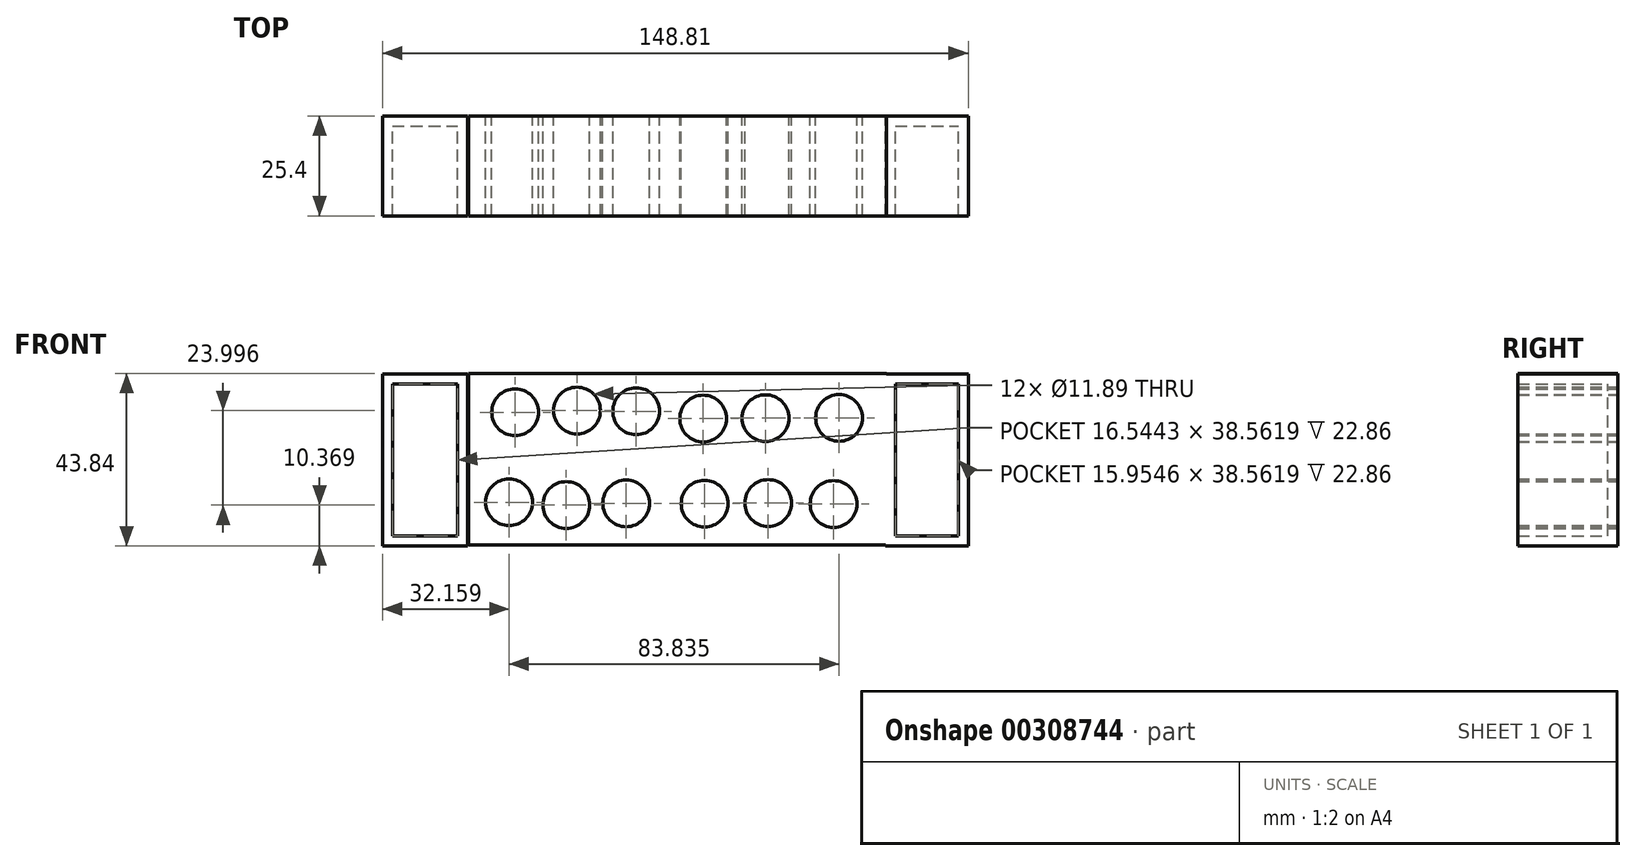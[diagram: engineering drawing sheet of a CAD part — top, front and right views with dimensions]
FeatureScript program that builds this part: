
annotation { "Feature Type Name" : "Feature", "Feature Type Description" : "" }
export const myFeature = defineFeature(function(context is Context, id is Id, definition is map)
    precondition{}
    {
        {
            var Q0;
            Q0=qCreatedBy(makeId("Front.planeOp"),FACE);
            var sketch = newSketch(context, id + "F0", { "sketchPlane" : qUnion([Q0])});
            skLineSegment(sketch, "E0", {"start": v(-61.92, 14.74) * mm, "end": v(86.9, 14.74) * mm});
            skLineSegment(sketch, "E1", {"start": v(86.9, 14.74) * mm, "end": v(86.9, -28.9) * mm});
            skLineSegment(sketch, "E2", {"start": v(86.9, -28.9) * mm, "end": v(-61.92, -28.9) * mm});
            skLineSegment(sketch, "E3", {"start": v(-61.92, -28.9) * mm, "end": v(-61.92, 14.74) * mm});
            skLineSegment(sketch, "E4", {"start": v(-40.3, 14.74) * mm, "end": v(-40.3, -28.9) * mm});
            skLineSegment(sketch, "E5", {"start": v(65.86, -28.9) * mm, "end": v(65.86, 14.74) * mm});
            skSolve(sketch);
        }
        {
            var Q0;
            {var subQ0=sQuery(id+"F0.wireOp",EDGE,"E3");Q0=makeQuery(id+"F0.imprint","IMPRINT",FACE,{"disambiguationData":[TD([[makeQuery(id+"F0.imprint","IMPRINT",EDGE,{"derivedFrom":subQ0}),-1.0]])]});}
            var Q1;
            {var subQ0=sQuery(id+"F0.wireOp",EDGE,"E1");Q1=makeQuery(id+"F0.imprint","IMPRINT",FACE,{"disambiguationData":[TD([[makeQuery(id+"F0.imprint","IMPRINT",EDGE,{"derivedFrom":subQ0}),-1.0]])]});}
            extrude(context, id + "F1", {"entities" : qUnion([Q0, Q1]), "depth" : 25.4 * mm});
        }
        {
            var Q0;
            Q0=makeQuery(id+"F1.opExtrude","CAP_FACE",FACE,{"disambiguationData":[OSD([sQuery(id+"F0.wireOp",EDGE,"E0"),sQuery(id+"F0.wireOp",EDGE,"E1"),sQuery(id+"F0.wireOp",EDGE,"E2"),sQuery(id+"F0.wireOp",EDGE,"E5")])],"isStart":false});
            var Q1;
            Q1=makeQuery(id+"F1.opExtrude","CAP_FACE",FACE,{"disambiguationData":[OSD([sQuery(id+"F0.wireOp",EDGE,"E0"),sQuery(id+"F0.wireOp",EDGE,"E2"),sQuery(id+"F0.wireOp",EDGE,"E3"),sQuery(id+"F0.wireOp",EDGE,"E4")])],"isStart":false});
            shell(context, id + "F2", {"entities" : qUnion([Q0, Q1]), "thickness" : 2.54 * mm});
        }
        {
            var Q0;
            Q0=qCreatedBy(makeId("Front.planeOp"),FACE);
            var sketch = newSketch(context, id + "F3", { "sketchPlane" : qUnion([Q0])});
            skLineSegment(sketch, "E6.bottom", {"start": v(-40.07, 14.94) * mm, "end": v(66.09, 14.94) * mm});
            skLineSegment(sketch, "E6.top", {"start": v(-40.07, -28.7) * mm, "end": v(66.09, -28.7) * mm});
            skLineSegment(sketch, "E6.left", {"start": v(-40.07, 14.94) * mm, "end": v(-40.07, -28.7) * mm});
            skLineSegment(sketch, "E6.right", {"start": v(66.09, 14.94) * mm, "end": v(66.09, -28.7) * mm});
            skSolve(sketch);
        }
        {
            var Q0;
            Q0=makeQuery(id+"F3.imprint","IMPRINT",FACE,{"disambiguationData":[TD([[makeQuery(id+"F3.imprint","IMPRINT",EDGE,{"derivedFrom":sQuery(id+"F3.wireOp",EDGE,"E6.bottom")}),-1.0]])]});
            extrude(context, id + "F4", {"entities" : qUnion([Q0]), "operationType" : NewBodyOperationType.ADD, "depth" : 25.4 * mm});
        }
        {
            var Q0;
            Q0=qCreatedBy(makeId("Front.planeOp"),FACE);
            var sketch = newSketch(context, id + "F5", { "sketchPlane" : qUnion([Q0])});
            skCircle(sketch, "E7", {"center": v(-28.22, 5.05) * mm, "radius": 5.94 * mm});
            skCircle(sketch, "E8", {"center": v(-12.51, 5.47) * mm, "radius": 5.94 * mm});
            skCircle(sketch, "E9", {"center": v(2.54, 5.3) * mm, "radius": 5.94 * mm});
            skCircle(sketch, "E10", {"center": v(19.56, 3.45) * mm, "radius": 5.94 * mm});
            skCircle(sketch, "E11", {"center": v(35.4, 3.55) * mm, "radius": 5.94 * mm});
            skCircle(sketch, "E12", {"center": v(54.07, 3.62) * mm, "radius": 5.94 * mm});
            skCircle(sketch, "E13", {"center": v(-29.76, -17.82) * mm, "radius": 5.94 * mm});
            skCircle(sketch, "E14", {"center": v(-15.23, -18.53) * mm, "radius": 5.94 * mm});
            skCircle(sketch, "E15", {"center": v(0, -18.08) * mm, "radius": 5.94 * mm});
            skCircle(sketch, "E16", {"center": v(19.92, -18.17) * mm, "radius": 5.94 * mm});
            skCircle(sketch, "E17", {"center": v(36.08, -18.02) * mm, "radius": 5.94 * mm});
            skCircle(sketch, "E18", {"center": v(52.68, -18.26) * mm, "radius": 5.94 * mm});
            skSolve(sketch);
        }
        {
            var Q0;
            Q0=makeQuery(id+"F5.imprint","IMPRINT",FACE,{"disambiguationData":[TD([[makeQuery(id+"F5.imprint","IMPRINT",EDGE,{"derivedFrom":sQuery(id+"F5.wireOp",EDGE,"E13")}),1.0]])]});
            var Q1;
            Q1=makeQuery(id+"F5.imprint","IMPRINT",FACE,{"disambiguationData":[TD([[makeQuery(id+"F5.imprint","IMPRINT",EDGE,{"derivedFrom":sQuery(id+"F5.wireOp",EDGE,"E14")}),1.0]])]});
            var Q2;
            Q2=makeQuery(id+"F5.imprint","IMPRINT",FACE,{"disambiguationData":[TD([[makeQuery(id+"F5.imprint","IMPRINT",EDGE,{"derivedFrom":sQuery(id+"F5.wireOp",EDGE,"E15")}),1.0]])]});
            var Q3;
            Q3=makeQuery(id+"F5.imprint","IMPRINT",FACE,{"disambiguationData":[TD([[makeQuery(id+"F5.imprint","IMPRINT",EDGE,{"derivedFrom":sQuery(id+"F5.wireOp",EDGE,"E16")}),1.0]])]});
            var Q4;
            Q4=makeQuery(id+"F5.imprint","IMPRINT",FACE,{"disambiguationData":[TD([[makeQuery(id+"F5.imprint","IMPRINT",EDGE,{"derivedFrom":sQuery(id+"F5.wireOp",EDGE,"E17")}),1.0]])]});
            var Q5;
            Q5=makeQuery(id+"F5.imprint","IMPRINT",FACE,{"disambiguationData":[TD([[makeQuery(id+"F5.imprint","IMPRINT",EDGE,{"derivedFrom":sQuery(id+"F5.wireOp",EDGE,"E18")}),1.0]])]});
            var Q6;
            Q6=makeQuery(id+"F5.imprint","IMPRINT",FACE,{"disambiguationData":[TD([[makeQuery(id+"F5.imprint","IMPRINT",EDGE,{"derivedFrom":sQuery(id+"F5.wireOp",EDGE,"E12")}),1.0]])]});
            var Q7;
            Q7=makeQuery(id+"F5.imprint","IMPRINT",FACE,{"disambiguationData":[TD([[makeQuery(id+"F5.imprint","IMPRINT",EDGE,{"derivedFrom":sQuery(id+"F5.wireOp",EDGE,"E11")}),1.0]])]});
            var Q8;
            Q8=makeQuery(id+"F5.imprint","IMPRINT",FACE,{"disambiguationData":[TD([[makeQuery(id+"F5.imprint","IMPRINT",EDGE,{"derivedFrom":sQuery(id+"F5.wireOp",EDGE,"E10")}),1.0]])]});
            var Q9;
            Q9=makeQuery(id+"F5.imprint","IMPRINT",FACE,{"disambiguationData":[TD([[makeQuery(id+"F5.imprint","IMPRINT",EDGE,{"derivedFrom":sQuery(id+"F5.wireOp",EDGE,"E9")}),1.0]])]});
            var Q10;
            Q10=makeQuery(id+"F5.imprint","IMPRINT",FACE,{"disambiguationData":[TD([[makeQuery(id+"F5.imprint","IMPRINT",EDGE,{"derivedFrom":sQuery(id+"F5.wireOp",EDGE,"E8")}),1.0]])]});
            var Q11;
            Q11=makeQuery(id+"F5.imprint","IMPRINT",FACE,{"disambiguationData":[TD([[makeQuery(id+"F5.imprint","IMPRINT",EDGE,{"derivedFrom":sQuery(id+"F5.wireOp",EDGE,"E7")}),1.0]])]});
            extrude(context, id + "F6", {"entities" : qUnion([Q0, Q1, Q2, Q3, Q4, Q5, Q6, Q7, Q8, Q9, Q10, Q11]), "operationType" : NewBodyOperationType.REMOVE, "depth" : 75.18 * mm});
        }
    });
